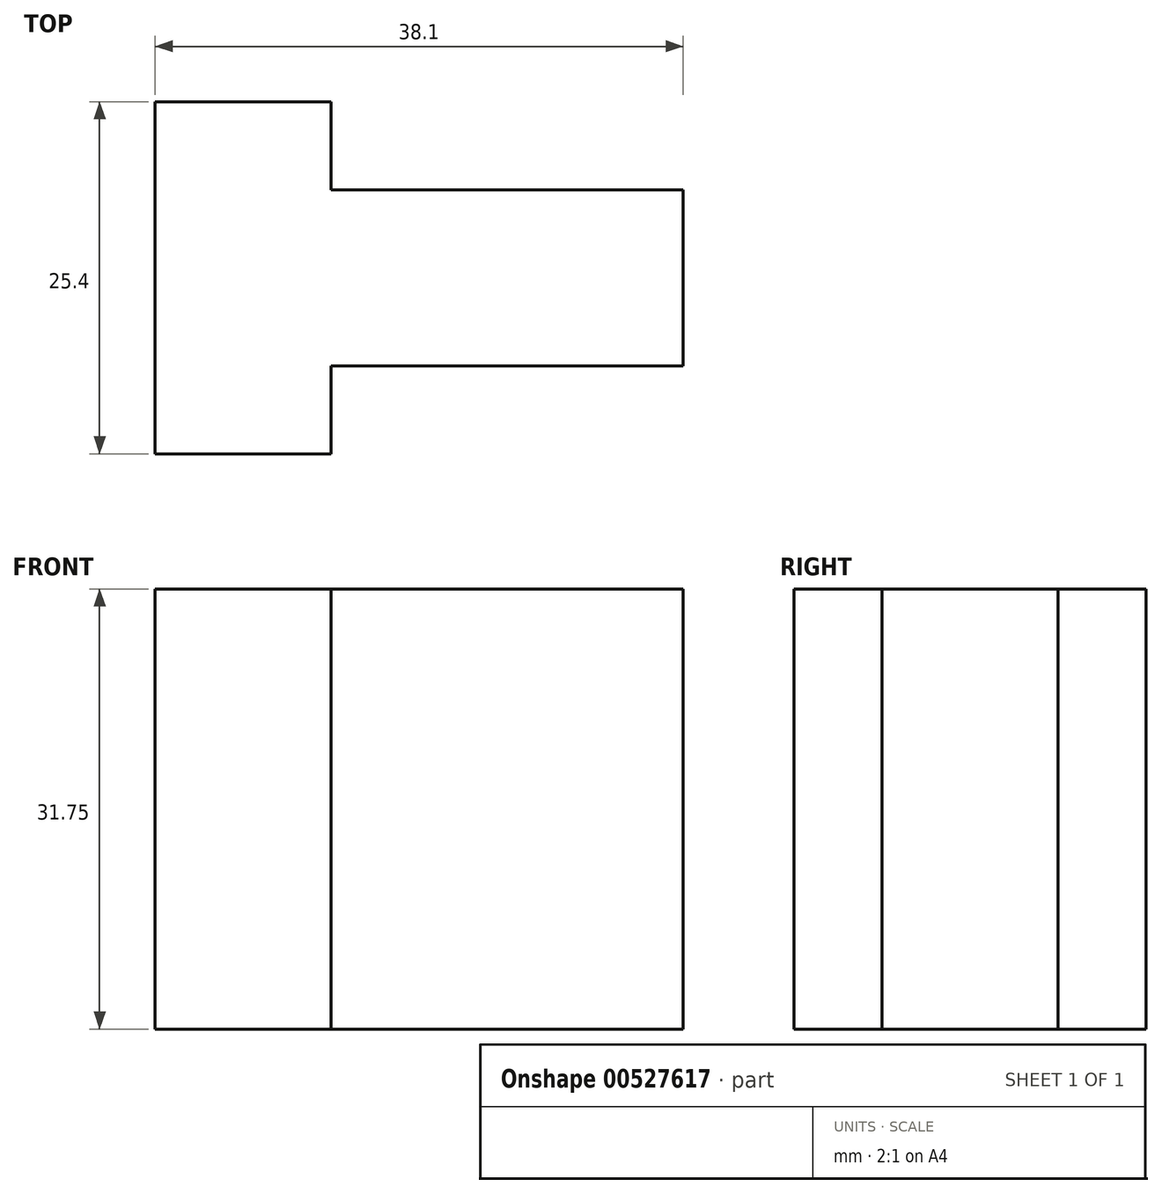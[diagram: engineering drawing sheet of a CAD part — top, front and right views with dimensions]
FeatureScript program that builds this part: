
annotation { "Feature Type Name" : "Feature", "Feature Type Description" : "" }
export const myFeature = defineFeature(function(context is Context, id is Id, definition is map)
    precondition{}
    {
        {
            var Q0;
            Q0=qCreatedBy(makeId("Top.planeOp"),FACE);
            var sketch = newSketch(context, id + "F0", { "sketchPlane" : qUnion([Q0])});
            skLineSegment(sketch, "E0", {"start": v(0, 0) * mm, "end": v(12.7, 0) * mm});
            skLineSegment(sketch, "E1", {"start": v(12.7, 0) * mm, "end": v(12.7, 6.35) * mm});
            skLineSegment(sketch, "E2", {"start": v(12.7, 6.35) * mm, "end": v(38.1, 6.35) * mm});
            skLineSegment(sketch, "E3", {"start": v(38.1, 6.35) * mm, "end": v(38.1, 19.05) * mm});
            skLineSegment(sketch, "E4", {"start": v(38.1, 19.05) * mm, "end": v(12.7, 19.05) * mm});
            skLineSegment(sketch, "E5", {"start": v(12.7, 19.05) * mm, "end": v(12.7, 25.4) * mm});
            skLineSegment(sketch, "E6", {"start": v(12.7, 25.4) * mm, "end": v(0, 25.4) * mm});
            skLineSegment(sketch, "E7", {"start": v(0, 0) * mm, "end": v(0, 25.4) * mm});
            skSolve(sketch);
        }
        {
            var Q0;
            Q0=makeQuery(id+"F0.imprint","IMPRINT",FACE,{"disambiguationData":[TD([[makeQuery(id+"F0.imprint","IMPRINT",EDGE,{"derivedFrom":sQuery(id+"F0.wireOp",EDGE,"E0")}),1.0]])]});
            extrude(context, id + "F1", {"entities" : qUnion([Q0]), "depth" : 31.75 * mm, "offsetDistance" : 25.4 * mm});
        }
    });
